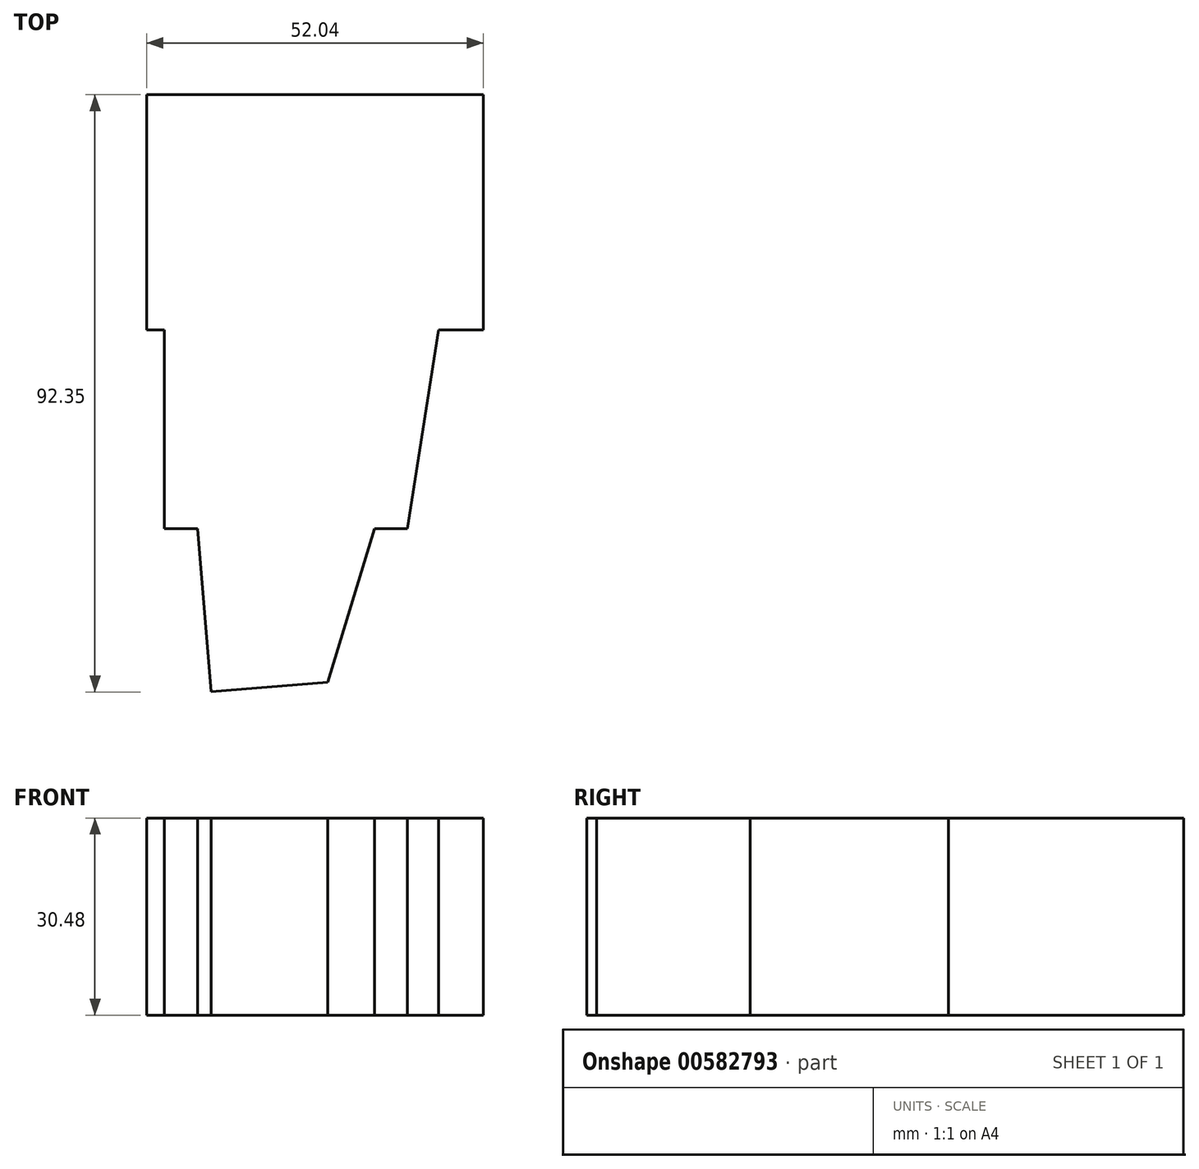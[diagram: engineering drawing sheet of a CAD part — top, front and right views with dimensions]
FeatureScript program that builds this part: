
annotation { "Feature Type Name" : "Feature", "Feature Type Description" : "" }
export const myFeature = defineFeature(function(context is Context, id is Id, definition is map)
    precondition{}
    {
        {
            var Q0;
            Q0=qCreatedBy(makeId("Top.planeOp"),FACE);
            var sketch = newSketch(context, id + "F0", { "sketchPlane" : qUnion([Q0])});
            skLineSegment(sketch, "E0", {"start": v(-67.53, 15.19) * mm, "end": v(-67.53, 51.59) * mm});
            skLineSegment(sketch, "E1", {"start": v(-67.53, 15.19) * mm, "end": v(-15.5, 15.19) * mm});
            skLineSegment(sketch, "E2", {"start": v(-15.5, 15.19) * mm, "end": v(-15.5, 51.59) * mm});
            skLineSegment(sketch, "E3", {"start": v(-67.53, 51.59) * mm, "end": v(-15.5, 51.59) * mm});
            skLineSegment(sketch, "E4", {"start": v(-64.82, 15.19) * mm, "end": v(-64.82, -15.5) * mm});
            skLineSegment(sketch, "E5", {"start": v(-64.82, -15.5) * mm, "end": v(-27.22, -15.5) * mm});
            skLineSegment(sketch, "E6", {"start": v(-27.22, -15.5) * mm, "end": v(-22.4, 15.19) * mm});
            skLineSegment(sketch, "E7", {"start": v(-59.7, -15.5) * mm, "end": v(-57.6, -40.76) * mm});
            skLineSegment(sketch, "E8", {"start": v(-57.6, -40.76) * mm, "end": v(-39.53, -39.25) * mm});
            skLineSegment(sketch, "E9", {"start": v(-39.53, -39.25) * mm, "end": v(-32.29, -15.5) * mm});
            skSolve(sketch);
        }
        {
            var Q0;
            {var subQ0=sQuery(id+"F0.wireOp",EDGE,"E7");Q0=makeQuery(id+"F0.imprint","IMPRINT",FACE,{"disambiguationData":[TD([[makeQuery(id+"F0.imprint","IMPRINT",EDGE,{"derivedFrom":subQ0}),1.0]])]});}
            var Q1;
            {var subQ3=sQuery(id+"F0.wireOp",EDGE,"E4");Q1=makeQuery(id+"F0.imprint","IMPRINT",FACE,{"disambiguationData":[TD([[makeQuery(id+"F0.imprint","IMPRINT",EDGE,{"derivedFrom":subQ3}),1.0]])]});}
            var Q2;
            {var subQ4=sQuery(id+"F0.wireOp",EDGE,"E0");Q2=makeQuery(id+"F0.imprint","IMPRINT",FACE,{"disambiguationData":[TD([[makeQuery(id+"F0.imprint","IMPRINT",EDGE,{"derivedFrom":subQ4}),-1.0]])]});}
            extrude(context, id + "F1", {"entities" : qUnion([Q0, Q1, Q2]), "depth" : 30.48 * mm, "offsetDistance" : 30.48 * mm});
        }
    });
